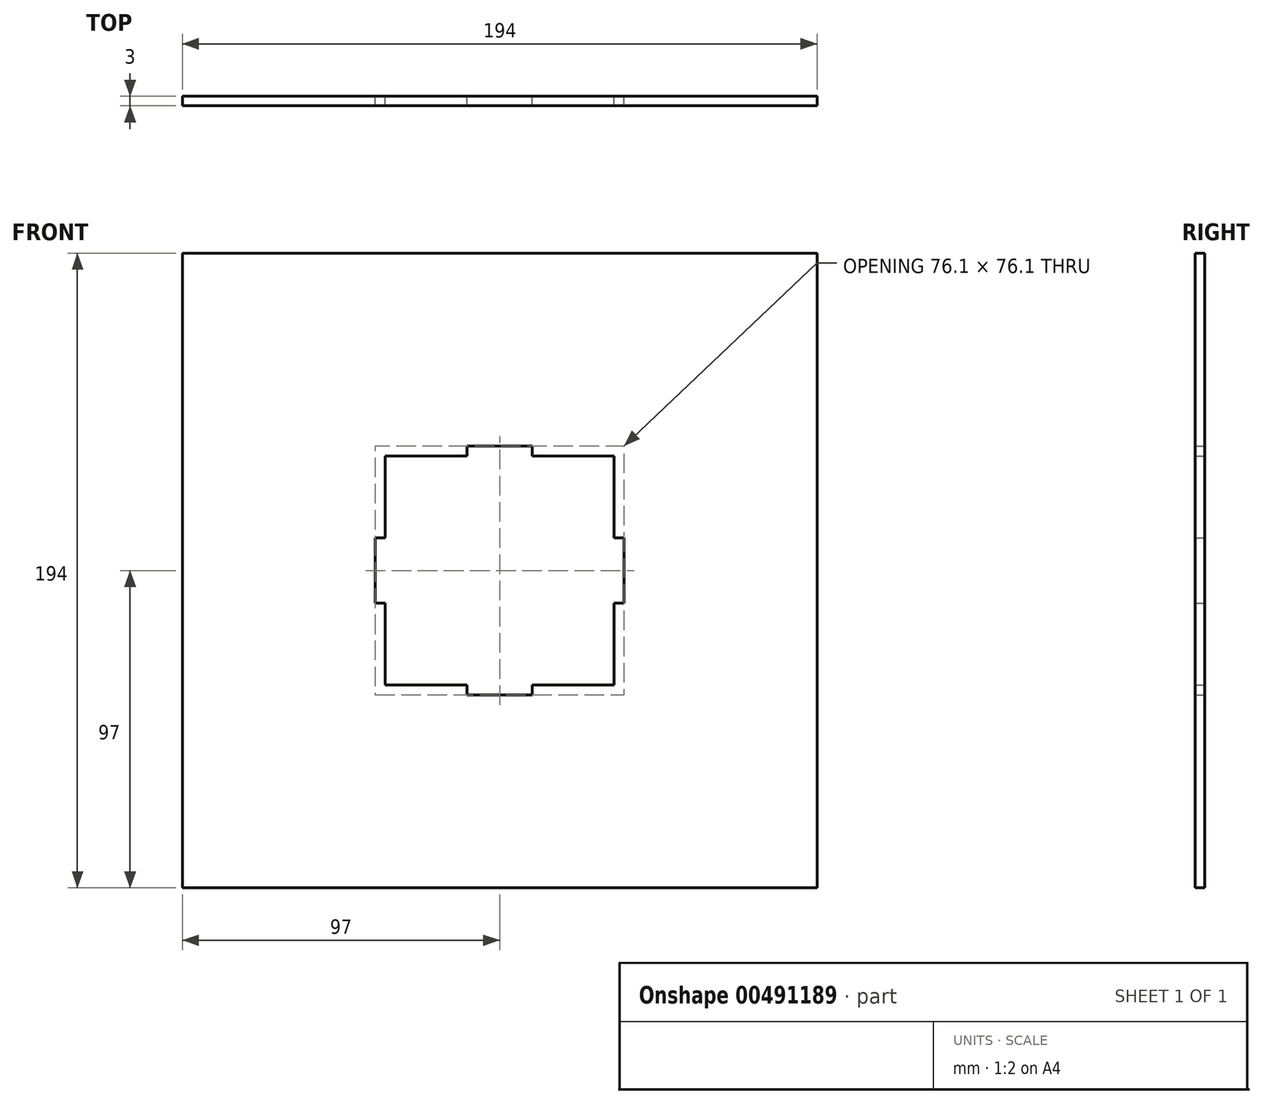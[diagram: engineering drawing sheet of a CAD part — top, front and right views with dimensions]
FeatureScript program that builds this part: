
annotation { "Feature Type Name" : "Feature", "Feature Type Description" : "" }
export const myFeature = defineFeature(function(context is Context, id is Id, definition is map)
    precondition{}
    {
        {
            var Q0;
            Q0=qCreatedBy(makeId("Front.planeOp"),FACE);
            var sketch = newSketch(context, id + "F0", { "sketchPlane" : qUnion([Q0])});
            skLineSegment(sketch, "E0.bottom", {"start": v(97, -97) * mm, "end": v(-97, -97) * mm});
            skLineSegment(sketch, "E0.top", {"start": v(97, 97) * mm, "end": v(-97, 97) * mm});
            skLineSegment(sketch, "E0.left", {"start": v(97, -97) * mm, "end": v(97, 97) * mm});
            skLineSegment(sketch, "E0.right", {"start": v(-97, -97) * mm, "end": v(-97, 97) * mm});
            skPoint(sketch, "E0.middle", {"position": v(0, 0) * mm});
            skLineSegment(sketch, "E1.bottom", {"start": v(35, -35) * mm, "end": v(-35, -35) * mm});
            skLineSegment(sketch, "E1.top", {"start": v(35, 35) * mm, "end": v(-35, 35) * mm});
            skLineSegment(sketch, "E1.left", {"start": v(35, -35) * mm, "end": v(35, 35) * mm});
            skLineSegment(sketch, "E1.right", {"start": v(-35, -35) * mm, "end": v(-35, 35) * mm});
            skLineSegment(sketch, "E2.bottom", {"start": v(-35, -9.95) * mm, "end": v(-38.05, -9.95) * mm});
            skLineSegment(sketch, "E2.top", {"start": v(-35, 9.95) * mm, "end": v(-38.05, 9.95) * mm});
            skLineSegment(sketch, "E2.left", {"start": v(-35, -9.95) * mm, "end": v(-35, 9.95) * mm});
            skLineSegment(sketch, "E2.right", {"start": v(-38.05, -9.95) * mm, "end": v(-38.05, 9.95) * mm});
            skPoint(sketch, "E2.middle", {"position": v(-36.52, 0) * mm});
            skLineSegment(sketch, "E3.bottom", {"start": v(38.05, -9.95) * mm, "end": v(35, -9.95) * mm});
            skLineSegment(sketch, "E3.top", {"start": v(38.05, 9.95) * mm, "end": v(35, 9.95) * mm});
            skLineSegment(sketch, "E3.left", {"start": v(38.05, -9.95) * mm, "end": v(38.05, 9.95) * mm});
            skLineSegment(sketch, "E3.right", {"start": v(35, -9.95) * mm, "end": v(35, 9.95) * mm});
            skPoint(sketch, "E3.middle", {"position": v(36.53, 0) * mm});
            skLineSegment(sketch, "E4.bottom", {"start": v(9.95, 38.05) * mm, "end": v(-9.95, 38.05) * mm});
            skLineSegment(sketch, "E4.top", {"start": v(9.95, 35) * mm, "end": v(-9.95, 35) * mm});
            skLineSegment(sketch, "E4.left", {"start": v(9.95, 38.05) * mm, "end": v(9.95, 35) * mm});
            skLineSegment(sketch, "E4.right", {"start": v(-9.95, 38.05) * mm, "end": v(-9.95, 35) * mm});
            skPoint(sketch, "E4.middle", {"position": v(0, 36.52) * mm});
            skLineSegment(sketch, "E5.bottom", {"start": v(9.95, -38.05) * mm, "end": v(-9.95, -38.05) * mm});
            skLineSegment(sketch, "E5.top", {"start": v(9.95, -35) * mm, "end": v(-9.95, -35) * mm});
            skLineSegment(sketch, "E5.left", {"start": v(9.95, -38.05) * mm, "end": v(9.95, -35) * mm});
            skLineSegment(sketch, "E5.right", {"start": v(-9.95, -38.05) * mm, "end": v(-9.95, -35) * mm});
            skPoint(sketch, "E5.middle", {"position": v(0, -36.52) * mm});
            skSolve(sketch);
        }
        {
            var Q0;
            Q0=makeQuery(id+"F0.imprint","IMPRINT",FACE,{"disambiguationData":[TD([[makeQuery(id+"F0.imprint","IMPRINT",EDGE,{"derivedFrom":sQuery(id+"F0.wireOp",EDGE,"E0.top")}),1.0]])]});
            extrude(context, id + "F1", {"entities" : qUnion([Q0]), "depth" : 3 * mm});
        }
    });
